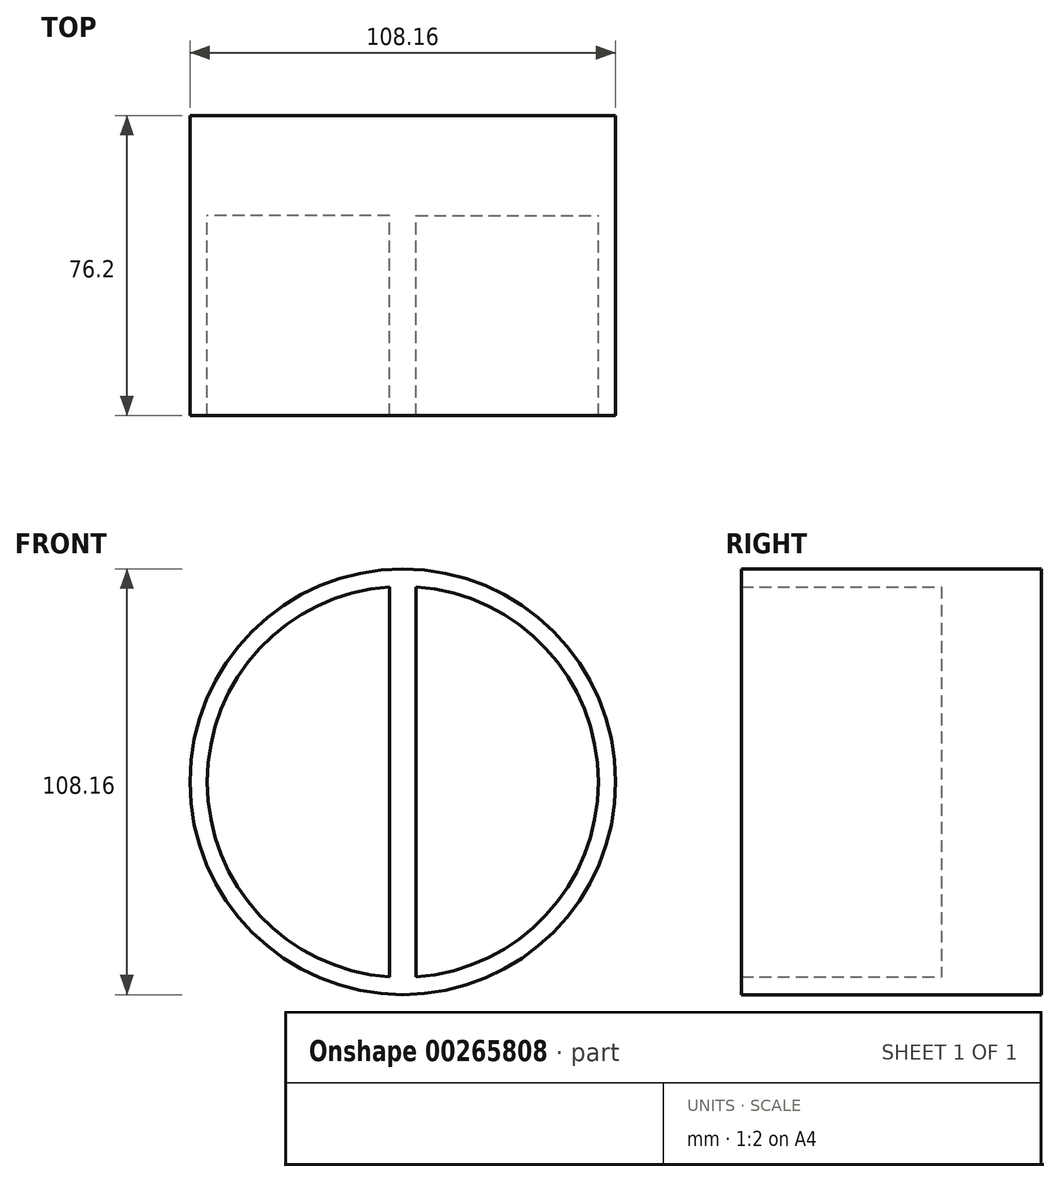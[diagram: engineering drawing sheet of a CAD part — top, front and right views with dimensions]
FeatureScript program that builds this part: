
annotation { "Feature Type Name" : "Feature", "Feature Type Description" : "" }
export const myFeature = defineFeature(function(context is Context, id is Id, definition is map)
    precondition{}
    {
        {
            var Q0;
            Q0=qCreatedBy(makeId("Front.planeOp"),FACE);
            var sketch = newSketch(context, id + "F0", { "sketchPlane" : qUnion([Q0])});
            skLineSegment(sketch, "E0.bottom", {"start": v(-3.43, 53.97) * mm, "end": v(3.43, 53.97) * mm});
            skLineSegment(sketch, "E0.top", {"start": v(-3.43, -53.97) * mm, "end": v(3.43, -53.97) * mm});
            skLineSegment(sketch, "E0.left", {"start": v(-3.43, 53.97) * mm, "end": v(-3.43, -53.97) * mm});
            skLineSegment(sketch, "E0.right", {"start": v(3.43, 53.97) * mm, "end": v(3.43, -53.97) * mm});
            skPoint(sketch, "E0.middle", {"position": v(0, 0) * mm});
            skCircle(sketch, "E1", {"center": v(0, 0) * mm, "radius": 54.08 * mm});
            skCircle(sketch, "E2", {"center": v(0, 0) * mm, "radius": 49.68 * mm});
            skSolve(sketch);
        }
        {
            var Q0;
            {var subQ0=sQuery(id+"F0.wireOp",EDGE,"E0.bottom");Q0=makeQuery(id+"F0.imprint","IMPRINT",FACE,{"disambiguationData":[TD([[makeQuery(id+"F0.imprint","IMPRINT",EDGE,{"derivedFrom":subQ0}),1.0]])]});}
            var Q1;
            {var subQ0=sQuery(id+"F0.wireOp",EDGE,"E0.top");Q1=makeQuery(id+"F0.imprint","IMPRINT",FACE,{"disambiguationData":[TD([[makeQuery(id+"F0.imprint","IMPRINT",EDGE,{"derivedFrom":subQ0}),-1.0]])]});}
            var Q2;
            {var subQ1=sQuery(id+"F0.wireOp",EDGE,"E0.right");var subQ3=sQuery(id+"F0.wireOp",EDGE,"E2");var subQ4=makeQuery(id+"F0.imprint","INTERSECT",VERTEX,{"disambiguationData":[OD(0.0)],"derivedFrom":[subQ1,subQ3]});Q2=makeQuery(id+"F0.imprint","IMPRINT",FACE,{"disambiguationData":[TD([[makeQuery(id+"F0.imprint","IMPRINT",EDGE,{"disambiguationData":[TD([[subQ4,1.0]])],"derivedFrom":subQ3}),-1.0]])]});}
            var Q3;
            {var subQ0=sQuery(id+"F0.wireOp",EDGE,"E0.bottom");Q3=makeQuery(id+"F0.imprint","IMPRINT",FACE,{"disambiguationData":[TD([[makeQuery(id+"F0.imprint","IMPRINT",EDGE,{"derivedFrom":subQ0}),-1.0]])]});}
            var Q4;
            {var subQ0=sQuery(id+"F0.wireOp",EDGE,"E0.top");Q4=makeQuery(id+"F0.imprint","IMPRINT",FACE,{"disambiguationData":[TD([[makeQuery(id+"F0.imprint","IMPRINT",EDGE,{"derivedFrom":subQ0}),1.0]])]});}
            var Q5;
            {var subQ1=sQuery(id+"F0.wireOp",EDGE,"E0.left");var subQ3=sQuery(id+"F0.wireOp",EDGE,"E2");var subQ4=makeQuery(id+"F0.imprint","INTERSECT",VERTEX,{"disambiguationData":[OD(0.0)],"derivedFrom":[subQ1,subQ3]});Q5=makeQuery(id+"F0.imprint","IMPRINT",FACE,{"disambiguationData":[TD([[makeQuery(id+"F0.imprint","IMPRINT",EDGE,{"disambiguationData":[TD([[subQ4,-1.0]])],"derivedFrom":subQ3}),-1.0]])]});}
            var Q6;
            {var subQ0=sQuery(id+"F0.wireOp",EDGE,"E2");var subQ1=sQuery(id+"F0.wireOp",EDGE,"E0.left");var subQ2=makeQuery(id+"F0.imprint","INTERSECT",VERTEX,{"disambiguationData":[OD(0.0)],"derivedFrom":[subQ1,subQ0]});Q6=makeQuery(id+"F0.imprint","IMPRINT",FACE,{"disambiguationData":[TD([[makeQuery(id+"F0.imprint","IMPRINT",EDGE,{"disambiguationData":[TD([[subQ2,-1.0]])],"derivedFrom":subQ1}),1.0]])]});}
            extrude(context, id + "F1", {"entities" : qUnion([Q0, Q1, Q2, Q3, Q4, Q5, Q6]), "depth" : 76.2 * mm});
        }
        {
            var Q0;
            {var subQ0=sQuery(id+"F0.wireOp",EDGE,"E2");var subQ1=sQuery(id+"F0.wireOp",EDGE,"E0.left");var subQ2=makeQuery(id+"F0.imprint","INTERSECT",VERTEX,{"disambiguationData":[OD(0.0)],"derivedFrom":[subQ1,subQ0]});Q0=makeQuery(id+"F0.imprint","IMPRINT",FACE,{"disambiguationData":[TD([[makeQuery(id+"F0.imprint","IMPRINT",EDGE,{"disambiguationData":[TD([[subQ2,-1.0]])],"derivedFrom":subQ1}),-1.0]])]});}
            var Q1;
            {var subQ0=sQuery(id+"F0.wireOp",EDGE,"E2");var subQ1=sQuery(id+"F0.wireOp",EDGE,"E0.right");var subQ2=makeQuery(id+"F0.imprint","INTERSECT",VERTEX,{"disambiguationData":[OD(0.0)],"derivedFrom":[subQ1,subQ0]});Q1=makeQuery(id+"F0.imprint","IMPRINT",FACE,{"disambiguationData":[TD([[makeQuery(id+"F0.imprint","IMPRINT",EDGE,{"disambiguationData":[TD([[subQ2,-1.0]])],"derivedFrom":subQ1}),1.0]])]});}
            extrude(context, id + "F2", {"entities" : qUnion([Q0, Q1]), "operationType" : NewBodyOperationType.ADD, "depth" : 25.4 * mm});
        }
    });
